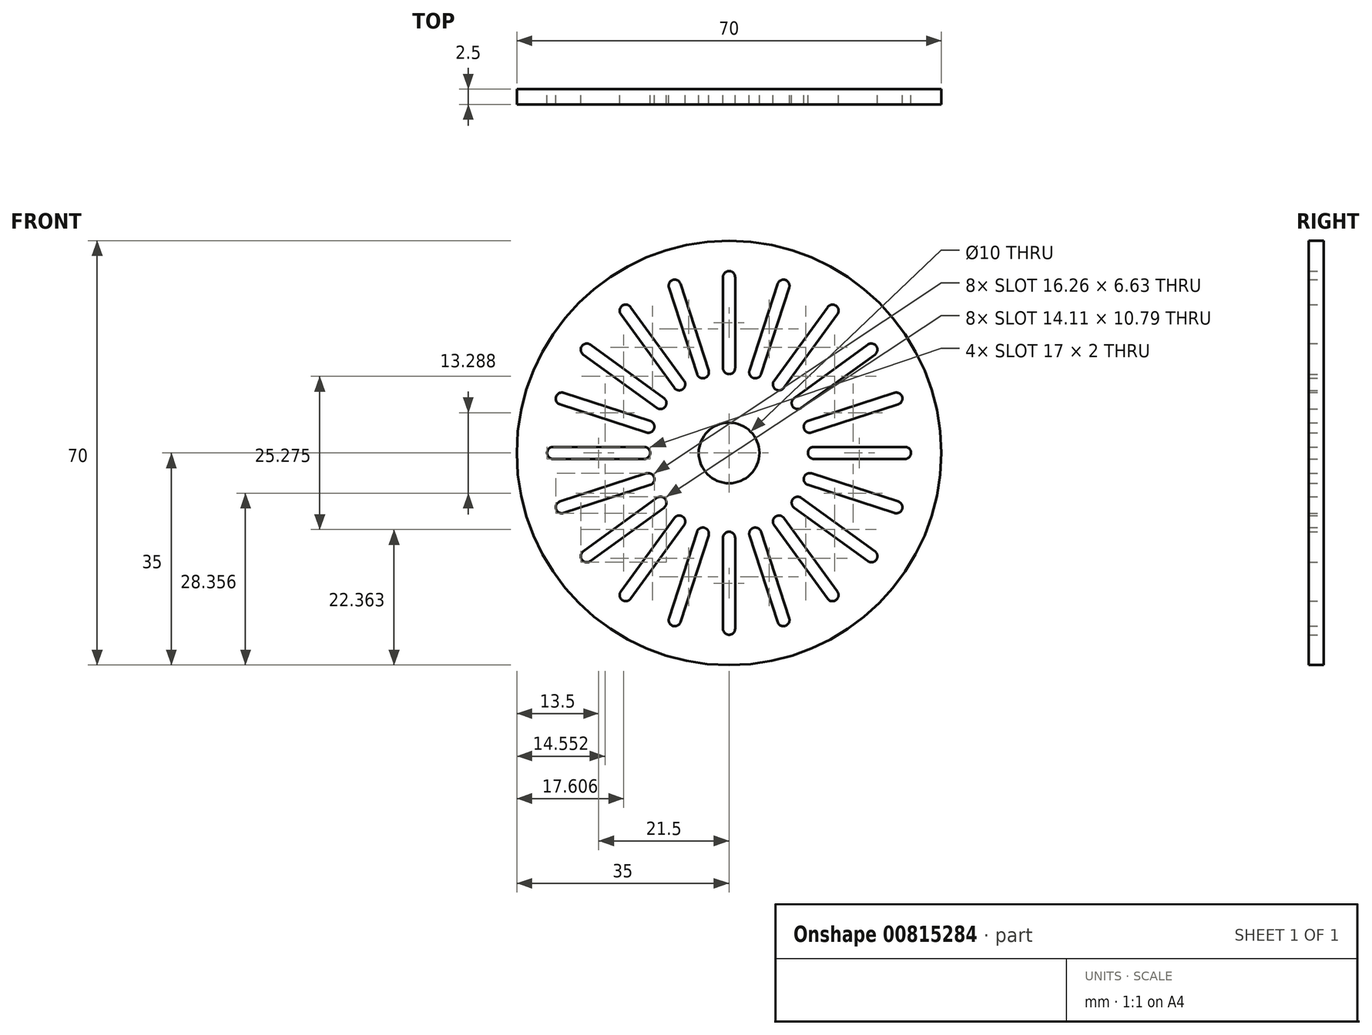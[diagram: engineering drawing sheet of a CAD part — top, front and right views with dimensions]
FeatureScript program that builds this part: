
annotation { "Feature Type Name" : "Feature", "Feature Type Description" : "" }
export const myFeature = defineFeature(function(context is Context, id is Id, definition is map)
    precondition{}
    {
        {
            var Q0;
            Q0=qCreatedBy(makeId("Front.planeOp"),FACE);
            var sketch = newSketch(context, id + "F0", { "sketchPlane" : qUnion([Q0])});
            skCircle(sketch, "E0", {"center": v(0, 0) * mm, "radius": 35 * mm});
            skCircle(sketch, "E1", {"center": v(0, 0) * mm, "radius": 5 * mm});
            skLineSegment(sketch, "E2", {"start": v(0, 29) * mm, "end": v(0, 14) * mm});
            skArc(sketch, "E3.0.startCap", {"start": v(-1, 29) * mm, "mid": v(0, 30) * mm, "end": v(1, 29) * mm});
            skArc(sketch, "E3.0.endCap", {"start": v(1, 14) * mm, "mid": v(0, 13) * mm, "end": v(-1, 14) * mm});
            skLineSegment(sketch, "E3.0.left", {"start": v(1, 29) * mm, "end": v(1, 14) * mm});
            skLineSegment(sketch, "E3.0.right", {"start": v(-1, 29) * mm, "end": v(-1, 14) * mm});
            skLineSegment(sketch, "E4.1.0", {"start": v(-9.91, 27.27) * mm, "end": v(-5.28, 13) * mm});
            skArc(sketch, "E4.1.1", {"start": v(-9.91, 27.27) * mm, "mid": v(-9.27, 28.53) * mm, "end": v(-8.01, 27.89) * mm});
            skLineSegment(sketch, "E4.1.2", {"start": v(-8.01, 27.89) * mm, "end": v(-3.38, 13.62) * mm});
            skArc(sketch, "E4.1.3", {"start": v(-3.38, 13.62) * mm, "mid": v(-4.02, 12.36) * mm, "end": v(-5.28, 13) * mm});
            skLineSegment(sketch, "E4.2.0", {"start": v(-17.85, 22.87) * mm, "end": v(-9.04, 10.74) * mm});
            skArc(sketch, "E4.2.1", {"start": v(-17.85, 22.87) * mm, "mid": v(-17.63, 24.27) * mm, "end": v(-16.24, 24.05) * mm});
            skLineSegment(sketch, "E4.2.2", {"start": v(-16.24, 24.05) * mm, "end": v(-7.42, 11.91) * mm});
            skArc(sketch, "E4.2.3", {"start": v(-7.42, 11.91) * mm, "mid": v(-7.64, 10.52) * mm, "end": v(-9.04, 10.74) * mm});
            skLineSegment(sketch, "E4.3.0", {"start": v(-24.05, 16.24) * mm, "end": v(-11.91, 7.42) * mm});
            skArc(sketch, "E4.3.1", {"start": v(-24.05, 16.24) * mm, "mid": v(-24.27, 17.63) * mm, "end": v(-22.87, 17.85) * mm});
            skLineSegment(sketch, "E4.3.2", {"start": v(-22.87, 17.85) * mm, "end": v(-10.74, 9.04) * mm});
            skArc(sketch, "E4.3.3", {"start": v(-10.74, 9.04) * mm, "mid": v(-10.52, 7.64) * mm, "end": v(-11.91, 7.42) * mm});
            skLineSegment(sketch, "E4.4.0", {"start": v(-27.89, 8.01) * mm, "end": v(-13.62, 3.38) * mm});
            skArc(sketch, "E4.4.1", {"start": v(-27.89, 8.01) * mm, "mid": v(-28.53, 9.27) * mm, "end": v(-27.27, 9.91) * mm});
            skLineSegment(sketch, "E4.4.2", {"start": v(-27.27, 9.91) * mm, "end": v(-13, 5.28) * mm});
            skArc(sketch, "E4.4.3", {"start": v(-13, 5.28) * mm, "mid": v(-12.36, 4.02) * mm, "end": v(-13.62, 3.38) * mm});
            skLineSegment(sketch, "E4.5.0", {"start": v(-29, -1) * mm, "end": v(-14, -1) * mm});
            skArc(sketch, "E4.5.1", {"start": v(-29, -1) * mm, "mid": v(-30, 0) * mm, "end": v(-29, 1) * mm});
            skLineSegment(sketch, "E4.5.2", {"start": v(-29, 1) * mm, "end": v(-14, 1) * mm});
            skArc(sketch, "E4.5.3", {"start": v(-14, 1) * mm, "mid": v(-13, 0) * mm, "end": v(-14, -1) * mm});
            skLineSegment(sketch, "E4.6.0", {"start": v(-27.27, -9.91) * mm, "end": v(-13, -5.28) * mm});
            skArc(sketch, "E4.6.1", {"start": v(-27.27, -9.91) * mm, "mid": v(-28.53, -9.27) * mm, "end": v(-27.89, -8.01) * mm});
            skLineSegment(sketch, "E4.6.2", {"start": v(-27.89, -8.01) * mm, "end": v(-13.62, -3.38) * mm});
            skArc(sketch, "E4.6.3", {"start": v(-13.62, -3.38) * mm, "mid": v(-12.36, -4.02) * mm, "end": v(-13, -5.28) * mm});
            skLineSegment(sketch, "E4.7.0", {"start": v(-22.87, -17.85) * mm, "end": v(-10.74, -9.04) * mm});
            skArc(sketch, "E4.7.1", {"start": v(-22.87, -17.85) * mm, "mid": v(-24.27, -17.63) * mm, "end": v(-24.05, -16.24) * mm});
            skLineSegment(sketch, "E4.7.2", {"start": v(-24.05, -16.24) * mm, "end": v(-11.91, -7.42) * mm});
            skArc(sketch, "E4.7.3", {"start": v(-11.91, -7.42) * mm, "mid": v(-10.52, -7.64) * mm, "end": v(-10.74, -9.04) * mm});
            skLineSegment(sketch, "E4.8.0", {"start": v(-16.24, -24.05) * mm, "end": v(-7.42, -11.91) * mm});
            skArc(sketch, "E4.8.1", {"start": v(-16.24, -24.05) * mm, "mid": v(-17.63, -24.27) * mm, "end": v(-17.85, -22.87) * mm});
            skLineSegment(sketch, "E4.8.2", {"start": v(-17.85, -22.87) * mm, "end": v(-9.04, -10.74) * mm});
            skArc(sketch, "E4.8.3", {"start": v(-9.04, -10.74) * mm, "mid": v(-7.64, -10.52) * mm, "end": v(-7.42, -11.91) * mm});
            skLineSegment(sketch, "E4.9.0", {"start": v(-8.01, -27.89) * mm, "end": v(-3.38, -13.62) * mm});
            skArc(sketch, "E4.9.1", {"start": v(-8.01, -27.89) * mm, "mid": v(-9.27, -28.53) * mm, "end": v(-9.91, -27.27) * mm});
            skLineSegment(sketch, "E4.9.2", {"start": v(-9.91, -27.27) * mm, "end": v(-5.28, -13) * mm});
            skArc(sketch, "E4.9.3", {"start": v(-5.28, -13) * mm, "mid": v(-4.02, -12.36) * mm, "end": v(-3.38, -13.62) * mm});
            skLineSegment(sketch, "E4.10.0", {"start": v(1, -29) * mm, "end": v(1, -14) * mm});
            skArc(sketch, "E4.10.1", {"start": v(1, -29) * mm, "mid": v(0, -30) * mm, "end": v(-1, -29) * mm});
            skLineSegment(sketch, "E4.10.2", {"start": v(-1, -29) * mm, "end": v(-1, -14) * mm});
            skArc(sketch, "E4.10.3", {"start": v(-1, -14) * mm, "mid": v(0, -13) * mm, "end": v(1, -14) * mm});
            skLineSegment(sketch, "E4.11.0", {"start": v(9.91, -27.27) * mm, "end": v(5.28, -13) * mm});
            skArc(sketch, "E4.11.1", {"start": v(9.91, -27.27) * mm, "mid": v(9.27, -28.53) * mm, "end": v(8.01, -27.89) * mm});
            skLineSegment(sketch, "E4.11.2", {"start": v(8.01, -27.89) * mm, "end": v(3.38, -13.62) * mm});
            skArc(sketch, "E4.11.3", {"start": v(3.38, -13.62) * mm, "mid": v(4.02, -12.36) * mm, "end": v(5.28, -13) * mm});
            skLineSegment(sketch, "E4.12.0", {"start": v(17.85, -22.87) * mm, "end": v(9.04, -10.74) * mm});
            skArc(sketch, "E4.12.1", {"start": v(17.85, -22.87) * mm, "mid": v(17.63, -24.27) * mm, "end": v(16.24, -24.05) * mm});
            skLineSegment(sketch, "E4.12.2", {"start": v(16.24, -24.05) * mm, "end": v(7.42, -11.91) * mm});
            skArc(sketch, "E4.12.3", {"start": v(7.42, -11.91) * mm, "mid": v(7.64, -10.52) * mm, "end": v(9.04, -10.74) * mm});
            skLineSegment(sketch, "E4.13.0", {"start": v(24.05, -16.24) * mm, "end": v(11.91, -7.42) * mm});
            skArc(sketch, "E4.13.1", {"start": v(24.05, -16.24) * mm, "mid": v(24.27, -17.63) * mm, "end": v(22.87, -17.85) * mm});
            skLineSegment(sketch, "E4.13.2", {"start": v(22.87, -17.85) * mm, "end": v(10.74, -9.04) * mm});
            skArc(sketch, "E4.13.3", {"start": v(10.74, -9.04) * mm, "mid": v(10.52, -7.64) * mm, "end": v(11.91, -7.42) * mm});
            skLineSegment(sketch, "E4.14.0", {"start": v(27.89, -8.01) * mm, "end": v(13.62, -3.38) * mm});
            skArc(sketch, "E4.14.1", {"start": v(27.89, -8.01) * mm, "mid": v(28.53, -9.27) * mm, "end": v(27.27, -9.91) * mm});
            skLineSegment(sketch, "E4.14.2", {"start": v(27.27, -9.91) * mm, "end": v(13, -5.28) * mm});
            skArc(sketch, "E4.14.3", {"start": v(13, -5.28) * mm, "mid": v(12.36, -4.02) * mm, "end": v(13.62, -3.38) * mm});
            skLineSegment(sketch, "E4.15.0", {"start": v(29, 1) * mm, "end": v(14, 1) * mm});
            skArc(sketch, "E4.15.1", {"start": v(29, 1) * mm, "mid": v(30, 0) * mm, "end": v(29, -1) * mm});
            skLineSegment(sketch, "E4.15.2", {"start": v(29, -1) * mm, "end": v(14, -1) * mm});
            skArc(sketch, "E4.15.3", {"start": v(14, -1) * mm, "mid": v(13, 0) * mm, "end": v(14, 1) * mm});
            skLineSegment(sketch, "E4.16.0", {"start": v(27.27, 9.91) * mm, "end": v(13, 5.28) * mm});
            skArc(sketch, "E4.16.1", {"start": v(27.27, 9.91) * mm, "mid": v(28.53, 9.27) * mm, "end": v(27.89, 8.01) * mm});
            skLineSegment(sketch, "E4.16.2", {"start": v(27.89, 8.01) * mm, "end": v(13.62, 3.38) * mm});
            skArc(sketch, "E4.16.3", {"start": v(13.62, 3.38) * mm, "mid": v(12.36, 4.02) * mm, "end": v(13, 5.28) * mm});
            skLineSegment(sketch, "E4.17.0", {"start": v(22.87, 17.85) * mm, "end": v(10.74, 9.04) * mm});
            skArc(sketch, "E4.17.1", {"start": v(22.87, 17.85) * mm, "mid": v(24.27, 17.63) * mm, "end": v(24.05, 16.24) * mm});
            skLineSegment(sketch, "E4.17.2", {"start": v(24.05, 16.24) * mm, "end": v(11.91, 7.42) * mm});
            skArc(sketch, "E4.17.3", {"start": v(11.91, 7.42) * mm, "mid": v(10.52, 7.64) * mm, "end": v(10.74, 9.04) * mm});
            skLineSegment(sketch, "E4.18.0", {"start": v(16.24, 24.05) * mm, "end": v(7.42, 11.91) * mm});
            skArc(sketch, "E4.18.1", {"start": v(16.24, 24.05) * mm, "mid": v(17.63, 24.27) * mm, "end": v(17.85, 22.87) * mm});
            skLineSegment(sketch, "E4.18.2", {"start": v(17.85, 22.87) * mm, "end": v(9.04, 10.74) * mm});
            skArc(sketch, "E4.18.3", {"start": v(9.04, 10.74) * mm, "mid": v(7.64, 10.52) * mm, "end": v(7.42, 11.91) * mm});
            skLineSegment(sketch, "E4.19.0", {"start": v(8.01, 27.89) * mm, "end": v(3.38, 13.62) * mm});
            skArc(sketch, "E4.19.1", {"start": v(8.01, 27.89) * mm, "mid": v(9.27, 28.53) * mm, "end": v(9.91, 27.27) * mm});
            skLineSegment(sketch, "E4.19.2", {"start": v(9.91, 27.27) * mm, "end": v(5.28, 13) * mm});
            skArc(sketch, "E4.19.3", {"start": v(5.28, 13) * mm, "mid": v(4.02, 12.36) * mm, "end": v(3.38, 13.62) * mm});
            skSolve(sketch);
        }
        {
            var Q0;
            Q0=makeQuery(id+"F0.imprint","IMPRINT",FACE,{"disambiguationData":[TD([[makeQuery(id+"F0.imprint","IMPRINT",EDGE,{"derivedFrom":sQuery(id+"F0.wireOp",EDGE,"E0")}),1.0]])]});
            extrude(context, id + "F1", {"entities" : qUnion([Q0]), "depth" : 2.5 * mm, "offsetDistance" : 25 * mm, "symmetric" : true});
        }
    });
